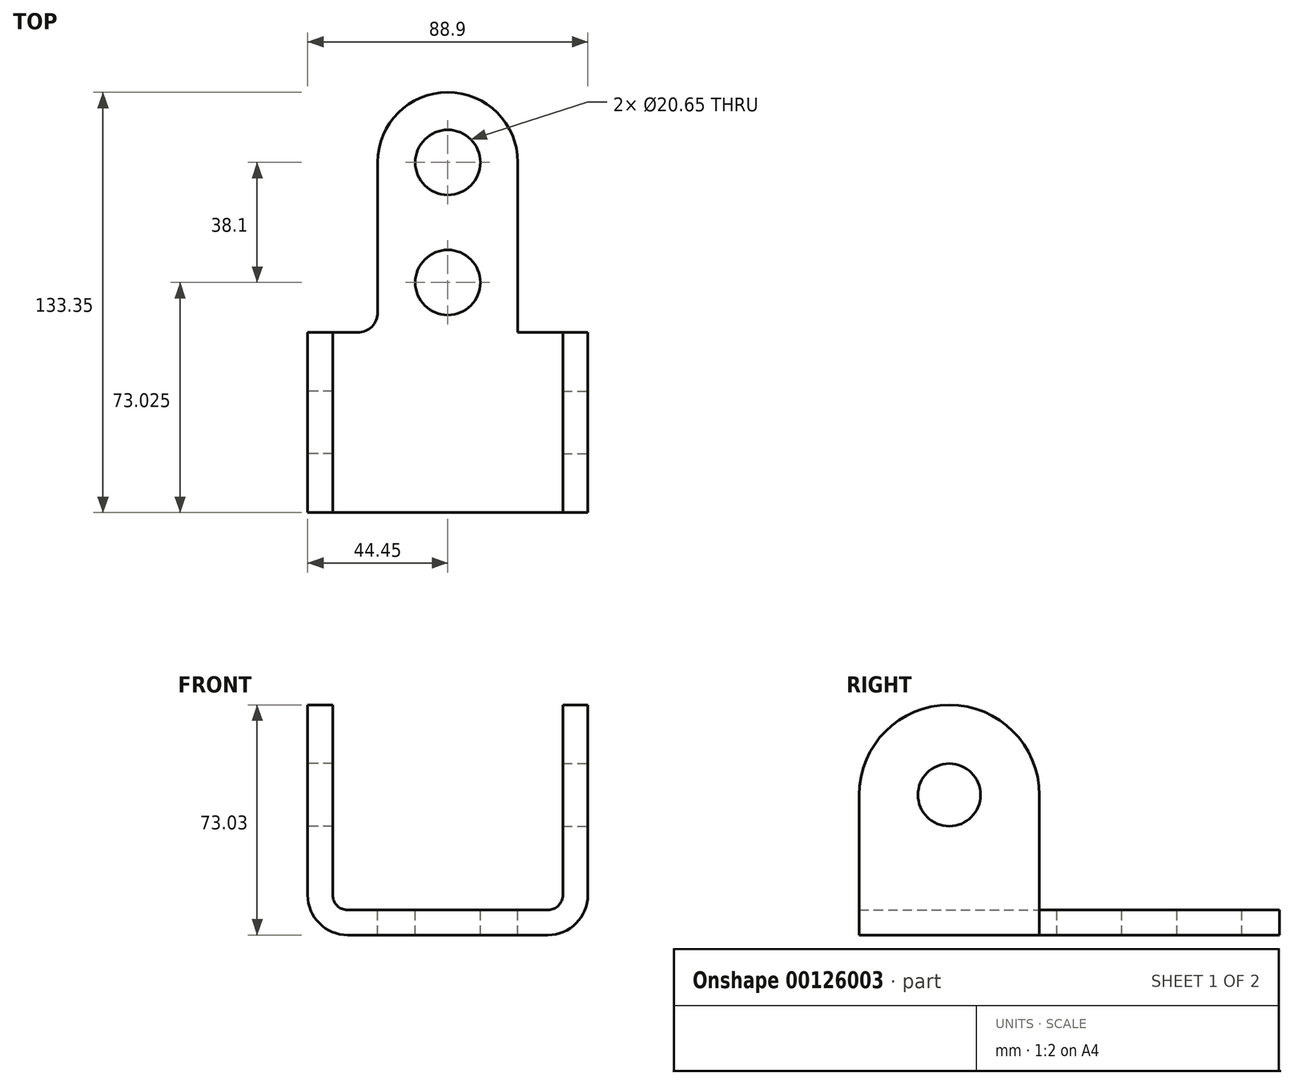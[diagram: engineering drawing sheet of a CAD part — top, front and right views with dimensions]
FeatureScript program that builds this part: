
annotation { "Feature Type Name" : "Feature", "Feature Type Description" : "" }
export const myFeature = defineFeature(function(context is Context, id is Id, definition is map)
    precondition{}
    {
        {
            var Q0;
            Q0=qCreatedBy(makeId("Front.planeOp"),FACE);
            var sketch = newSketch(context, id + "F0", { "sketchPlane" : qUnion([Q0])});
            skLineSegment(sketch, "E0", {"start": v(0, 0) * mm, "end": v(31.75, 0) * mm});
            skLineSegment(sketch, "E1", {"start": v(0, 0) * mm, "end": v(-31.75, 0) * mm});
            skLineSegment(sketch, "E2", {"start": v(44.45, 12.7) * mm, "end": v(44.45, 44.45) * mm});
            skLineSegment(sketch, "E3", {"start": v(-44.45, 12.7) * mm, "end": v(-44.45, 44.45) * mm});
            skLineSegment(sketch, "E4", {"start": v(-44.45, 44.45) * mm, "end": v(-36.51, 44.45) * mm});
            skLineSegment(sketch, "E5", {"start": v(-36.51, 44.45) * mm, "end": v(-36.51, 12.7) * mm});
            skLineSegment(sketch, "E6", {"start": v(-31.75, 7.94) * mm, "end": v(31.75, 7.94) * mm});
            skLineSegment(sketch, "E7", {"start": v(36.51, 12.7) * mm, "end": v(36.51, 44.46) * mm});
            skLineSegment(sketch, "E8", {"start": v(36.51, 44.46) * mm, "end": v(44.45, 44.45) * mm});
            skPoint(sketch, "E9.visualSharp", {"position": v(-44.45, 0) * mm});
            skArc(sketch, "E9.filletArc", {"start": v(-44.45, 12.7) * mm, "mid": v(-40.73, 3.72) * mm, "end": v(-31.75, 0) * mm});
            skPoint(sketch, "E10.visualSharp", {"position": v(-36.51, 7.94) * mm});
            skArc(sketch, "E10.filletArc", {"start": v(-36.51, 12.7) * mm, "mid": v(-35.12, 9.33) * mm, "end": v(-31.75, 7.94) * mm});
            skPoint(sketch, "E11.visualSharp", {"position": v(36.51, 7.94) * mm});
            skArc(sketch, "E11.filletArc", {"start": v(31.75, 7.94) * mm, "mid": v(35.12, 9.33) * mm, "end": v(36.51, 12.7) * mm});
            skPoint(sketch, "E12.visualSharp", {"position": v(44.45, 0) * mm});
            skArc(sketch, "E12.filletArc", {"start": v(31.75, 0) * mm, "mid": v(40.73, 3.72) * mm, "end": v(44.45, 12.7) * mm});
            skSolve(sketch);
        }
        {
            var Q0;
            Q0 = qSketchRegion(id + "F0", true);
            extrude(context, id + "F1", {"entities" : qUnion([Q0]), "depth" : 57.15 * mm});
        }
        {
            var Q0;
            Q0=makeQuery(id+"F1.opExtrude","SWEPT_FACE",FACE,{"disambiguationData":[OSD([sQuery(id+"F0.wireOp",EDGE,"E2")])]});
            var sketch = newSketch(context, id + "F2", { "sketchPlane" : qUnion([Q0])});
            skArc(sketch, "E13", {"start": v(-57.15, 44.45) * mm, "mid": v(-28.58, 73.02) * mm, "end": v(0, 44.45) * mm});
            skCircle(sketch, "E14", {"center": v(-28.58, 44.45) * mm, "radius": 9.92 * mm});
            skLineSegment(sketch, "E15", {"start": v(-57.15, 44.45) * mm, "end": v(-38.5, 44.45) * mm});
            skLineSegment(sketch, "E16", {"start": v(-18.65, 44.45) * mm, "end": v(0, 44.45) * mm});
            skSolve(sketch);
        }
        {
            var Q0;
            Q0 = qSketchRegion(id + "F2", true);
            var Q1;
            Q1=makeQuery(id+"F1.opExtrude","SWEPT_FACE",FACE,{"disambiguationData":[OSD([sQuery(id+"F0.wireOp",EDGE,"E7")])]});
            extrude(context, id + "F3", {"entities" : qUnion([Q0]), "operationType" : NewBodyOperationType.ADD, "endBound" : BoundingType.UP_TO_SURFACE, "oppositeDirection" : true, "endBoundEntityFace" : qUnion([Q1]), "depth" : 25.4 * mm});
        }
        {
            var Q0;
            {var subQ0=sQuery(id+"F2.wireOp",EDGE,"E14");var subQ1=makeQuery(id+"F1.opExtrude","SWEPT_EDGE",EDGE,{"disambiguationData":[OSD([sQuery(id+"F0.wireOp",EDGE,"E2"),sQuery(id+"F0.wireOp",EDGE,"E8")])]});var subQ2=makeQuery(id+"F2.imprint","INTERSECT",VERTEX,{"derivedFrom":[subQ1,subQ0,sQuery(id+"F2.wireOp",EDGE,"E15")]});Q0=makeQuery(id+"F2.imprint","IMPRINT",FACE,{"disambiguationData":[TD([[makeQuery(id+"F2.imprint","IMPRINT",EDGE,{"disambiguationData":[TD([[subQ2,1.0]])],"derivedFrom":subQ0}),1.0]])]});}
            var Q1;
            {var subQ0=sQuery(id+"F2.wireOp",EDGE,"E14");var subQ1=makeQuery(id+"F1.opExtrude","SWEPT_EDGE",EDGE,{"disambiguationData":[OSD([sQuery(id+"F0.wireOp",EDGE,"E2"),sQuery(id+"F0.wireOp",EDGE,"E8")])]});var subQ2=makeQuery(id+"F2.imprint","INTERSECT",VERTEX,{"derivedFrom":[subQ1,subQ0,sQuery(id+"F2.wireOp",EDGE,"E15")]});Q1=makeQuery(id+"F2.imprint","IMPRINT",FACE,{"disambiguationData":[TD([[makeQuery(id+"F2.imprint","IMPRINT",EDGE,{"disambiguationData":[TD([[subQ2,-1.0]])],"derivedFrom":subQ0}),1.0]])]});}
            var Q2;
            Q2=sQuery(id+"F2.wireOp",EDGE,"E14");
            var Q3;
            {var subQ0=sQuery(id+"F0.wireOp",EDGE,"E7");Q3=makeQuery(id+"F3.boolean.opBoolean","MERGE",FACE,{"derivedFrom":[makeQuery(id+"F1.opExtrude","SWEPT_FACE",FACE,{"disambiguationData":[OSD([subQ0])]}),makeQuery(id+"F3.opExtrude","CAP_FACE",FACE,{"disambiguationData":[OSD([subQ0])],"isStart":false})]});}
            extrude(context, id + "F4", {"entities" : qUnion([Q0, Q1]), "operationType" : NewBodyOperationType.REMOVE, "surfaceEntities" : qUnion([Q2]), "endBound" : BoundingType.UP_TO_SURFACE, "oppositeDirection" : true, "endBoundEntityFace" : qUnion([Q3]), "depth" : 25.4 * mm});
        }
        {
            var Q0;
            Q0=makeQuery(id+"F1.opExtrude","SWEPT_FACE",FACE,{"disambiguationData":[OSD([sQuery(id+"F0.wireOp",EDGE,"E3")])]});
            var sketch = newSketch(context, id + "F5", { "sketchPlane" : qUnion([Q0])});
            skArc(sketch, "E17", {"start": v(0, 44.45) * mm, "mid": v(28.58, 73.03) * mm, "end": v(57.15, 44.45) * mm});
            skCircle(sketch, "E18", {"center": v(28.58, 44.45) * mm, "radius": 9.92 * mm});
            skLineSegment(sketch, "E19", {"start": v(0, 44.45) * mm, "end": v(18.65, 44.45) * mm});
            skLineSegment(sketch, "E20", {"start": v(57.15, 44.45) * mm, "end": v(38.5, 44.45) * mm});
            skSolve(sketch);
        }
        {
            var Q0;
            Q0 = qSketchRegion(id + "F5", true);
            var Q1;
            Q1=makeQuery(id+"F1.opExtrude","SWEPT_FACE",FACE,{"disambiguationData":[OSD([sQuery(id+"F0.wireOp",EDGE,"E5")])]});
            extrude(context, id + "F6", {"entities" : qUnion([Q0]), "operationType" : NewBodyOperationType.ADD, "endBound" : BoundingType.UP_TO_SURFACE, "oppositeDirection" : true, "endBoundEntityFace" : qUnion([Q1]), "depth" : 25.4 * mm});
        }
        {
            var Q0;
            {var subQ0=sQuery(id+"F5.wireOp",EDGE,"E18");var subQ1=makeQuery(id+"F1.opExtrude","SWEPT_EDGE",EDGE,{"disambiguationData":[OSD([sQuery(id+"F0.wireOp",EDGE,"E3"),sQuery(id+"F0.wireOp",EDGE,"E4")])]});var subQ2=makeQuery(id+"F5.imprint","INTERSECT",VERTEX,{"derivedFrom":[subQ1,subQ0,sQuery(id+"F5.wireOp",EDGE,"E19")]});Q0=makeQuery(id+"F5.imprint","IMPRINT",FACE,{"disambiguationData":[TD([[makeQuery(id+"F5.imprint","IMPRINT",EDGE,{"disambiguationData":[TD([[subQ2,-1.0]])],"derivedFrom":subQ0}),1.0]])]});}
            var Q1;
            {var subQ0=sQuery(id+"F5.wireOp",EDGE,"E18");var subQ1=makeQuery(id+"F1.opExtrude","SWEPT_EDGE",EDGE,{"disambiguationData":[OSD([sQuery(id+"F0.wireOp",EDGE,"E3"),sQuery(id+"F0.wireOp",EDGE,"E4")])]});var subQ2=makeQuery(id+"F5.imprint","INTERSECT",VERTEX,{"derivedFrom":[subQ1,subQ0,sQuery(id+"F5.wireOp",EDGE,"E19")]});Q1=makeQuery(id+"F5.imprint","IMPRINT",FACE,{"disambiguationData":[TD([[makeQuery(id+"F5.imprint","IMPRINT",EDGE,{"disambiguationData":[TD([[subQ2,1.0]])],"derivedFrom":subQ0}),1.0]])]});}
            var Q2;
            {var subQ0=sQuery(id+"F0.wireOp",EDGE,"E5");Q2=makeQuery(id+"F6.boolean.opBoolean","MERGE",FACE,{"derivedFrom":[makeQuery(id+"F1.opExtrude","SWEPT_FACE",FACE,{"disambiguationData":[OSD([subQ0])]}),makeQuery(id+"F6.opExtrude","CAP_FACE",FACE,{"disambiguationData":[OSD([subQ0])],"isStart":false})]});}
            extrude(context, id + "F7", {"entities" : qUnion([Q0, Q1]), "operationType" : NewBodyOperationType.REMOVE, "endBound" : BoundingType.UP_TO_SURFACE, "oppositeDirection" : true, "endBoundEntityFace" : qUnion([Q2]), "depth" : 25.4 * mm});
        }
        {
            var Q0;
            Q0=makeQuery(id+"F1.opExtrude","SWEPT_FACE",FACE,{"disambiguationData":[OSD([sQuery(id+"F0.wireOp",EDGE,"E6")])]});
            var sketch = newSketch(context, id + "F8", { "sketchPlane" : qUnion([Q0])});
            skLineSegment(sketch, "E21", {"start": v(0, 0) * mm, "end": v(0, 15.88) * mm, "construction": true});
            skLineSegment(sketch, "E22", {"start": v(0, 15.88) * mm, "end": v(0, 53.98) * mm, "construction": true});
            skCircle(sketch, "E23", {"center": v(0, 53.98) * mm, "radius": 10.33 * mm});
            skCircle(sketch, "E24", {"center": v(0, 15.88) * mm, "radius": 10.33 * mm});
            skArc(sketch, "E25", {"start": v(-22.23, 53.97) * mm, "mid": v(0, 76.2) * mm, "end": v(22.23, 53.98) * mm});
            skLineSegment(sketch, "E26", {"start": v(-22.23, 53.97) * mm, "end": v(-22.23, 0) * mm});
            skLineSegment(sketch, "E27", {"start": v(22.23, 53.97) * mm, "end": v(22.23, 0) * mm});
            skLineSegment(sketch, "E28", {"start": v(22.23, 0) * mm, "end": v(-22.23, 0) * mm});
            skSolve(sketch);
        }
        {
            var Q0;
            Q0 = qSketchRegion(id + "F8", true);
            var Q1;
            Q1=makeQuery(id+"F1.opExtrude","SWEPT_FACE",FACE,{"disambiguationData":[OSD([sQuery(id+"F0.wireOp",EDGE,"E0"),sQuery(id+"F0.wireOp",EDGE,"E1")])]});
            extrude(context, id + "F9", {"entities" : qUnion([Q0]), "operationType" : NewBodyOperationType.ADD, "endBound" : BoundingType.UP_TO_SURFACE, "oppositeDirection" : true, "endBoundEntityFace" : qUnion([Q1]), "depth" : 25.4 * mm});
        }
        {
            var Q0;
            Q0=makeQuery(id+"F9.opExtrude","SWEPT_EDGE",EDGE,{"disambiguationData":[OSD([sQuery(id+"F0.wireOp",EDGE,"E6"),sQuery(id+"F8.wireOp",EDGE,"E27"),sQuery(id+"F8.wireOp",EDGE,"E28")])]});
            var Q1;
            Q1=makeQuery(id+"F9.opExtrude","SWEPT_EDGE",EDGE,{"disambiguationData":[OSD([sQuery(id+"F0.wireOp",EDGE,"E6"),sQuery(id+"F8.wireOp",EDGE,"E26"),sQuery(id+"F8.wireOp",EDGE,"E28")])]});
            fillet(context, id + "F10", {"entities" : qUnion([Q0, Q1]), "radius" : 6.35 * mm, "tangentPropagation" : true, "allowEdgeOverflow" : false});
        }
    });
